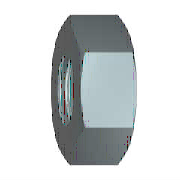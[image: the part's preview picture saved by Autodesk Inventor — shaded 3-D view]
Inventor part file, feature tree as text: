
AUTODESK INVENTOR PART (.ipt)
format: ipt  version: 2013 (Build 170138000, 138)  size: 161,280 bytes
history: native  units: mm (DEFAULTED — no unit token found)
features: sketch x3, chamfer x1, hole x1, other x1, plane x1
ambient origin geometry x7: Origin, YZ Plane, XZ Plane, X Axis, Y Axis, Z Axis, Center Point
bodies: Solid1 (feature_tree), Body (feature_tree)
feature tree (7):
  chamfer  "Chamfer1"  Angle=30.0deg  [1 undecoded]
  hole  "Thread"  [1 undecoded]
  other  "Work Axis1"
  plane  "Work Plane1"
  sketch  "Sketch1"  dims[d0=8.082904mm]
  sketch  "Sketch2"  dims[d1=3.2mm]
  sketch  "Sketch3"  dims[d2=0.0mm d3=30.0deg d4=30.0deg d5=5.9mm d6=5.9mm d7=90.0deg d25=3.242mm d26=6.0mm d27=4.0mm d28=2.0mm d29=14.3117mm d30=8.0mm d31=20.594885mm d8=0.378886mm d9=30.0deg d10=0.378886mm d11=30.0deg d13=0.0mm d14=0.0mm d39=0.0mm d40=0.378886mm d41=0.378886mm d42=0.0mm]
note: 2 required parameter values undecoded (feature->parameter linkage not recoverable at this tier; creation-order binding heuristic only, values carry confidence <= 0.55)
